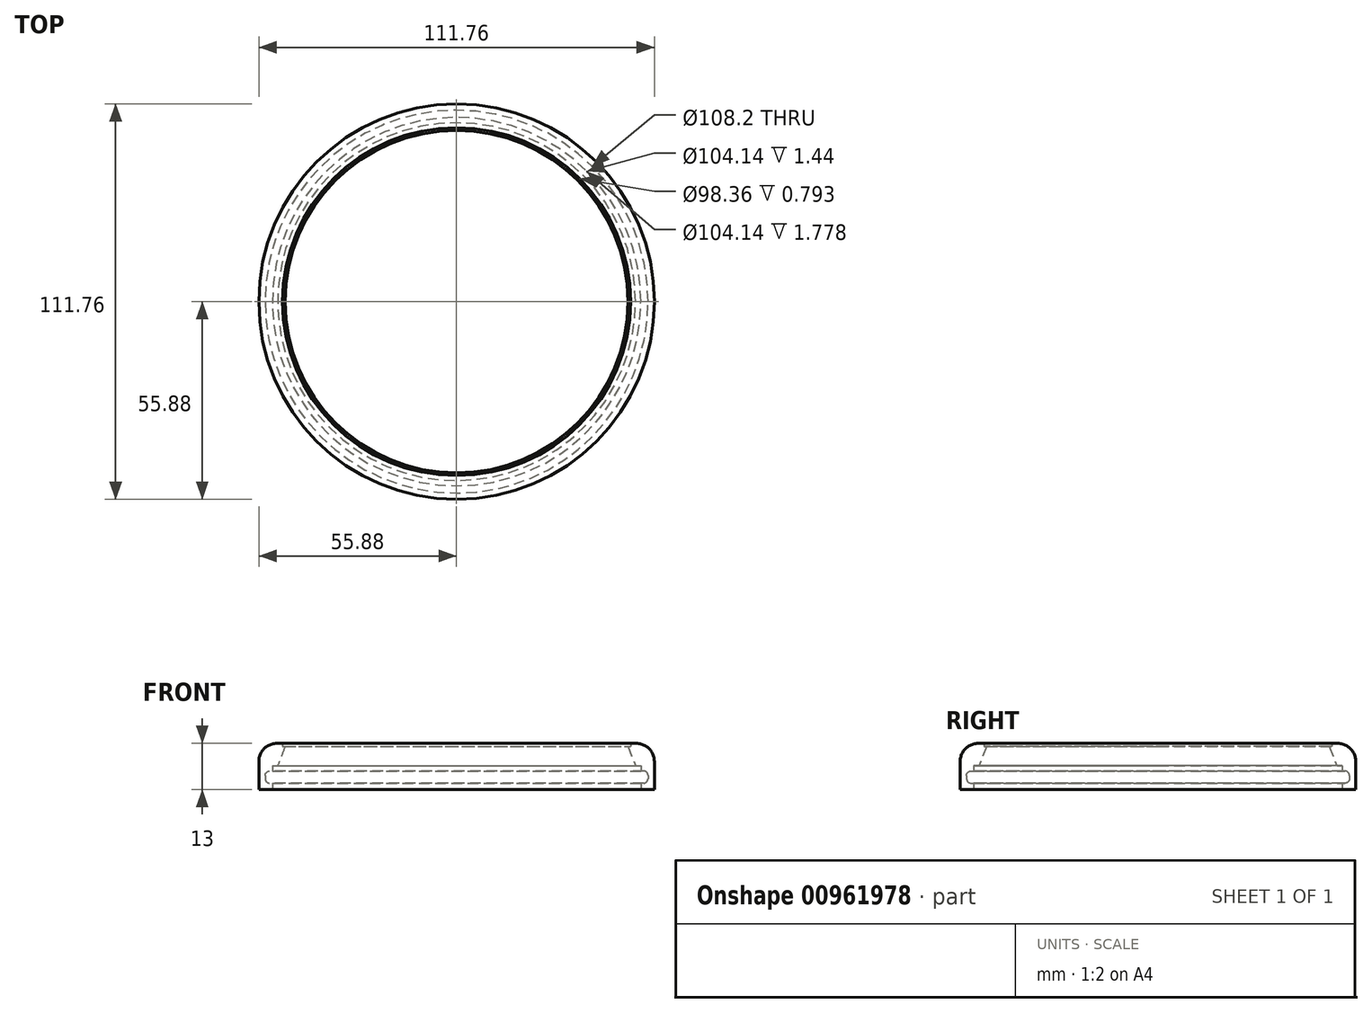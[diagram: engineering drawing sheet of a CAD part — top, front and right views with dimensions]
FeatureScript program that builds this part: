
annotation { "Feature Type Name" : "Feature", "Feature Type Description" : "" }
export const myFeature = defineFeature(function(context is Context, id is Id, definition is map)
    precondition{}
    {
        {
            var Q0;
            Q0=qCreatedBy(makeId("Front.planeOp"),FACE);
            var sketch = newSketch(context, id + "F0", { "sketchPlane" : qUnion([Q0])});
            skLineSegment(sketch, "E0", {"start": v(0, 0) * mm, "end": v(-16.51, 0) * mm});
            skLineSegment(sketch, "E1", {"start": v(-16.51, 0) * mm, "end": v(-41.66, 0) * mm});
            skLineSegment(sketch, "E2", {"start": v(0, 0) * mm, "end": v(0, 6.35) * mm});
            skLineSegment(sketch, "E3", {"start": v(0, 6.35) * mm, "end": v(-16.51, 6.35) * mm});
            skLineSegment(sketch, "E4", {"start": v(-16.51, 6.35) * mm, "end": v(-47, 6.35) * mm});
            skLineSegment(sketch, "E5", {"start": v(-47, 6.35) * mm, "end": v(-41.66, 0) * mm});
            skCircle(sketch, "E6", {"center": v(-49.01, -1.67) * mm, "radius": 1.59 * mm});
            skLineSegment(sketch, "E7", {"start": v(-54.1, -1.44) * mm, "end": v(-54.1, -4.87) * mm});
            skLineSegment(sketch, "E8", {"start": v(-54.1, -4.87) * mm, "end": v(-52.07, -4.87) * mm});
            skLineSegment(sketch, "E9", {"start": v(-52.07, -4.87) * mm, "end": v(-52.07, -6.65) * mm});
            skLineSegment(sketch, "E10", {"start": v(-52.07, -6.65) * mm, "end": v(-53.34, -6.65) * mm});
            skLineSegment(sketch, "E11", {"start": v(-53.34, -6.65) * mm, "end": v(-55.88, -6.65) * mm});
            skLineSegment(sketch, "E12", {"start": v(-55.88, -6.65) * mm, "end": v(-55.88, 6.35) * mm});
            skLineSegment(sketch, "E13", {"start": v(-55.88, 6.35) * mm, "end": v(-47, 6.35) * mm});
            skLineSegment(sketch, "E14", {"start": v(0, -15.02) * mm, "end": v(-47, -15.02) * mm});
            skLineSegment(sketch, "E15", {"start": v(-47, -15.02) * mm, "end": v(-47, 0) * mm});
            skLineSegment(sketch, "E16", {"start": v(-47, 6.35) * mm, "end": v(-47, -19.05) * mm});
            skLineSegment(sketch, "E17", {"start": v(-41.66, 0) * mm, "end": v(-41.66, -25.4) * mm});
            skLineSegment(sketch, "E18", {"start": v(-41.66, -25.4) * mm, "end": v(-46.99, -19.05) * mm});
            skLineSegment(sketch, "E19", {"start": v(0, 7.85) * mm, "end": v(-53.98, 7.85) * mm});
            skLineSegment(sketch, "E20", {"start": v(-41.66, -25.4) * mm, "end": v(-47, -25.4) * mm});
            skLineSegment(sketch, "E21", {"start": v(-47, -25.4) * mm, "end": v(-47, -19.05) * mm});
            skLineSegment(sketch, "E22", {"start": v(-47, 6.35) * mm, "end": v(-45.47, 6.35) * mm});
            skLineSegment(sketch, "E23", {"start": v(-45.47, 6.35) * mm, "end": v(-45.47, -25.4) * mm});
            skLineSegment(sketch, "E24", {"start": v(-54.1, -4.87) * mm, "end": v(-53.34, -6.65) * mm});
            skLineSegment(sketch, "E25", {"start": v(-47, 0) * mm, "end": v(-54.1, 0) * mm});
            skLineSegment(sketch, "E26", {"start": v(-54.1, 0) * mm, "end": v(-54.1, -1.44) * mm});
            skLineSegment(sketch, "E27", {"start": v(-47, 6.35) * mm, "end": v(-46.35, 6.35) * mm});
            skLineSegment(sketch, "E28", {"start": v(-46.35, 6.35) * mm, "end": v(-46.35, -25.4) * mm});
            skLineSegment(sketch, "E29", {"start": v(-52.07, -4.87) * mm, "end": v(-52.07, 0) * mm});
            skCircle(sketch, "E30", {"center": v(-46.35, -24.51) * mm, "radius": 0.89 * mm});
            skLineSegment(sketch, "E31", {"start": v(-46.35, -25.4) * mm, "end": v(-46.35, -24.51) * mm});
            skLineSegment(sketch, "E32", {"start": v(-47, 0) * mm, "end": v(-46.35, 0) * mm});
            skLineSegment(sketch, "E33", {"start": v(-50.42, 6.35) * mm, "end": v(-50.3, 6.35) * mm});
            skLineSegment(sketch, "E34", {"start": v(-50.3, 0) * mm, "end": v(-50.55, 0) * mm});
            skLineSegment(sketch, "E35", {"start": v(-54.1, -1.44) * mm, "end": v(-52.07, -1.44) * mm});
            skLineSegment(sketch, "E36", {"start": v(-50.55, 0) * mm, "end": v(-48.42, 5.56) * mm});
            skLineSegment(sketch, "E37", {"start": v(-48.42, 5.56) * mm, "end": v(-49.18, 5.56) * mm});
            skLineSegment(sketch, "E38", {"start": v(-49.18, 5.56) * mm, "end": v(-49.18, 6.35) * mm});
            skSolve(sketch);
        }
        {
            var Q0;
            Q0=makeQuery(id+"F0.imprint","IMPRINT",FACE,{"disambiguationData":[TD([[makeQuery(id+"F0.imprint","IMPRINT",EDGE,{"derivedFrom":sQuery(id+"F0.wireOp",EDGE,"E7")}),-1.0]])]});
            var Q1;
            Q1=makeQuery(id+"F0.imprint","IMPRINT",FACE,{"disambiguationData":[TD([[makeQuery(id+"F0.imprint","IMPRINT",EDGE,{"derivedFrom":sQuery(id+"F0.wireOp",EDGE,"E8")}),-1.0]])]});
            var Q2;
            {var subQ0=sQuery(id+"F0.wireOp",EDGE,"E26");Q2=makeQuery(id+"F0.imprint","IMPRINT",FACE,{"disambiguationData":[TD([[makeQuery(id+"F0.imprint","IMPRINT",EDGE,{"derivedFrom":subQ0}),1.0]])]});}
            var Q3;
            Q3=sQuery(id+"F0.wireOp",EDGE,"E2");
            revolve(context, id + "F1", {"surfaceOperationType" : NewSurfaceOperationType.NEW, "entities" : qUnion([Q0, Q1, Q2]), "axis" : qUnion([Q3]), "revolveType" : RevolveType.FULL});
        }
        {
            var Q0;
            Q0=makeQuery(id+"F1.opRevolve","SWEPT_EDGE",EDGE,{"disambiguationData":[OSD([sQuery(id+"F0.wireOp",EDGE,"E7"),sQuery(id+"F0.wireOp",EDGE,"E26"),sQuery(id+"F0.wireOp",EDGE,"E35")])]});
            var Q1;
            Q1=makeQuery(id+"F1.opRevolve","SWEPT_EDGE",EDGE,{"disambiguationData":[OSD([sQuery(id+"F0.wireOp",EDGE,"E7"),sQuery(id+"F0.wireOp",EDGE,"E8"),sQuery(id+"F0.wireOp",EDGE,"E24")])]});
            fillet(context, id + "F2", {"entities" : qUnion([Q0, Q1]), "radius" : 1.27 * mm, "tangentPropagation" : true, "allowEdgeOverflow" : false});
        }
        {
            var Q0;
            Q0=makeQuery(id+"F1.opRevolve","SWEPT_EDGE",EDGE,{"disambiguationData":[OSD([sQuery(id+"F0.wireOp",EDGE,"E12"),sQuery(id+"F0.wireOp",EDGE,"E13")])]});
            fillet(context, id + "F3", {"entities" : qUnion([Q0]), "radius" : 5.08 * mm, "tangentPropagation" : true, "allowEdgeOverflow" : false});
        }
    });
